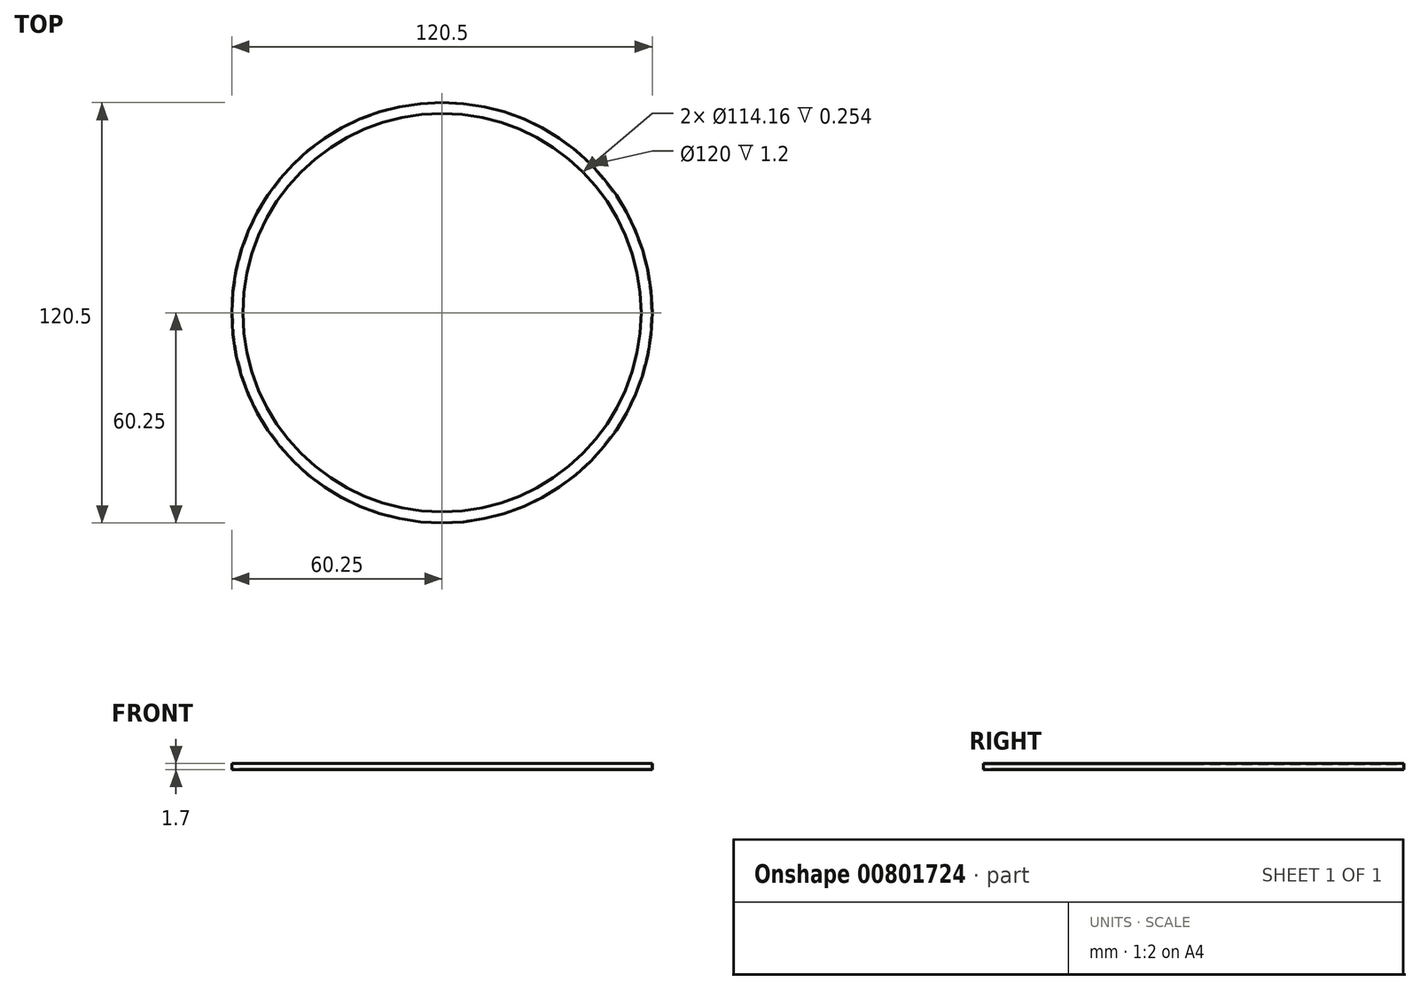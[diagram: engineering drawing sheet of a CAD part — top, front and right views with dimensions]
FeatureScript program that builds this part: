
annotation { "Feature Type Name" : "Feature", "Feature Type Description" : "" }
export const myFeature = defineFeature(function(context is Context, id is Id, definition is map)
    precondition{}
    {
        {
            var Q0;
            Q0=qCreatedBy(makeId("Top.planeOp"),FACE);
            var sketch = newSketch(context, id + "F0", { "sketchPlane" : qUnion([Q0])});
            skCircle(sketch, "E0", {"center": v(0, 0) * mm, "radius": 60.25 * mm});
            skCircle(sketch, "E1", {"center": v(0, 0) * mm, "radius": 57.08 * mm});
            skSolve(sketch);
        }
        {
            var Q0;
            Q0 = qSketchRegion(id + "F0", true);
            extrude(context, id + "F1", {"entities" : qUnion([Q0]), "depth" : 1.7 * mm, "offsetDistance" : 25.4 * mm, "symmetric" : true});
        }
        {
            var Q0;
            Q0=qCreatedBy(makeId("Top.planeOp"),FACE);
            var sketch = newSketch(context, id + "F2", { "sketchPlane" : qUnion([Q0])});
            skCircle(sketch, "E2", {"center": v(0, 0) * mm, "radius": 60 * mm});
            skSolve(sketch);
        }
        {
            var Q0;
            Q0 = qSketchRegion(id + "F2", true);
            extrude(context, id + "F3", {"entities" : qUnion([Q0]), "operationType" : NewBodyOperationType.REMOVE, "oppositeDirection" : true, "depth" : 1.2 * mm, "offsetDistance" : 25.4 * mm, "symmetric" : true});
        }
    });
